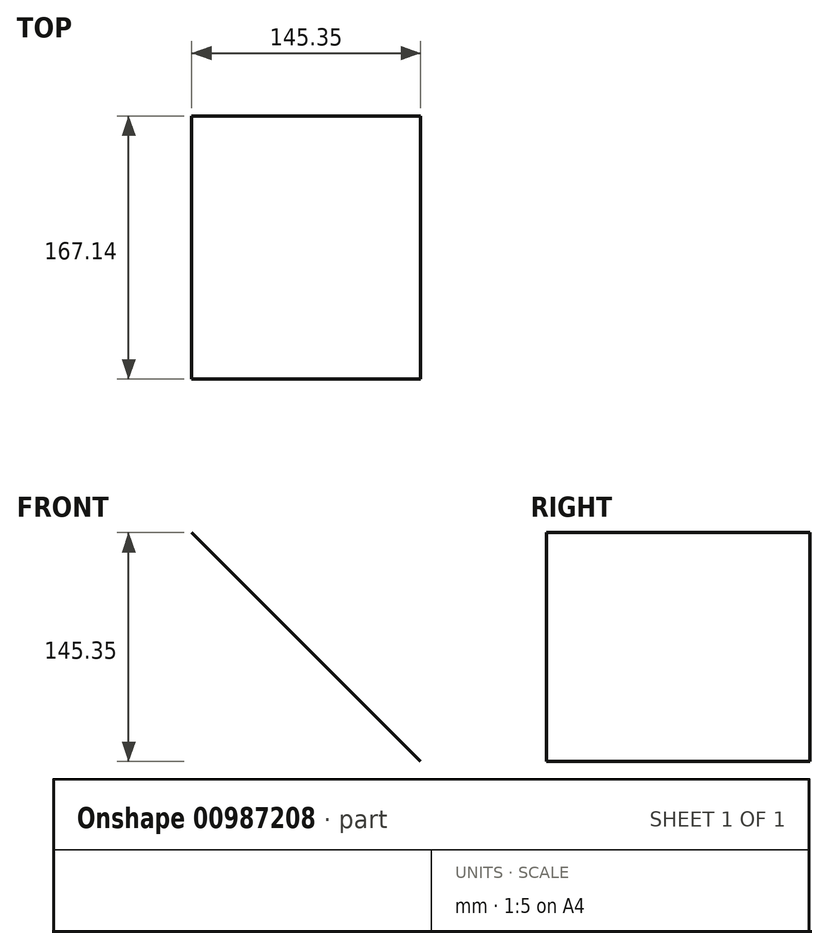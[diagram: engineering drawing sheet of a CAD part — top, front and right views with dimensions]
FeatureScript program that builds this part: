
annotation { "Feature Type Name" : "Feature", "Feature Type Description" : "" }
export const myFeature = defineFeature(function(context is Context, id is Id, definition is map)
    precondition{}
    {
        {
            var Q0;
            Q0=qCreatedBy(makeId("Front.planeOp"),FACE);
            var sketch = newSketch(context, id + "F0", { "sketchPlane" : qUnion([Q0])});
            skLineSegment(sketch, "E0", {"start": v(0, 145.35) * mm, "end": v(145.35, 0) * mm});
            skLineSegment(sketch, "E1", {"start": v(145.35, 0) * mm, "end": v(0, 0) * mm, "construction": true});
            skSolve(sketch);
        }
        {
            var Q0;
            Q0 = qSketchRegion(id + "F0", true);
            var Q1;
            Q1=sQuery(id+"F0.wireOp",EDGE,"E0");
            extrude(context, id + "F1", {"entities" : qUnion([Q0]), "bodyType" : ToolBodyType.SURFACE, "surfaceEntities" : qUnion([Q1]), "endBound" : BoundingType.SYMMETRIC, "depth" : 167.13 * mm, "offsetDistance" : 25.4 * mm});
        }
    });
